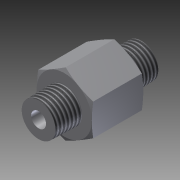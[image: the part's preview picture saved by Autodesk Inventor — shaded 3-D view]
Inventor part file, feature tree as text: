
AUTODESK INVENTOR PART (.ipt)
format: ipt  version: 2014 (Build 180170000, 170)  size: 142,336 bytes
history: native  units: in
note: dims shown in document units (in); Inventor stores cm internally (conversion verified against a paired STEP export)
features: sketch x4, extrude x3, plane x2, thread x2, other x1, hole x1, revolve x1, mirror x1, reference x1
ambient origin geometry x8: Origin, YZ Plane, XZ Plane, XY Plane, X Axis, Y Axis, Z Axis, Center Point
bodies: Solid1 (feature_tree)
feature tree (16):
  sketch  "Sketch1"  dims[d2=0.5in d3=0.0in d20=0.25in d21=-0.0123in]
  extrude  "Extrusion1"  Depth=0.25in
  plane  "Work Plane1"
  other  "Work Axis3"
  extrude  "Extrusion3"  Depth=0.25in
  thread  "Thread2"  [1 undecoded]
  hole  "Hole2"  [1 undecoded]
  extrude  "Extrusion4"  Depth=0.0414in
  thread  "Thread3"  [1 undecoded]
  revolve  "Revolution3"  [1 undecoded]
  plane  "Work Plane4"
  mirror  "Mirror4"
  sketch  "Sketch6"  dims[d22=0.392in d23=0.0in]
  reference  "Reference3"
  sketch  "Sketch7"  dims[d24=0.13in d25=0.75in d26=0.375in d27=0.25in d28=0.5635in d29=1.0in d30=0.8108in d31=0.25in d32=-0.0123in d33=0.392in d34=0.0in]
  sketch  "Sketch8"  dims[d35=90.0deg d36=0.5355in d37=0.0414in d38=0.0415in]
note: 4 required parameter values undecoded (feature->parameter linkage not recoverable at this tier; creation-order binding heuristic only, values carry confidence <= 0.55)
